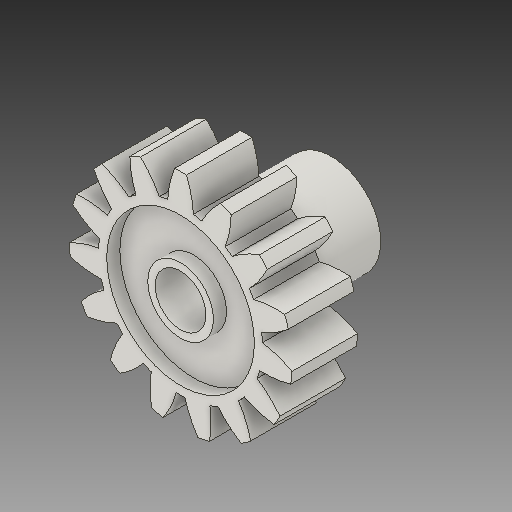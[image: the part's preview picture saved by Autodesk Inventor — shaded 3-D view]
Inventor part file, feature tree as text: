
AUTODESK INVENTOR PART (.ipt)
format: ipt  version: 2019 (Build 230136000, 136)  size: 214,016 bytes
history: imported  units: mm
features: imported_body x1
ambient origin geometry x8: Origin, YZ Plane, XZ Plane, XY Plane, X Axis, Y Axis, Z Axis, Center Point
bodies: Solide1 (imported_parasolid), Solid1 (imported_parasolid)
feature tree (1):
  imported_body  NMx_Import_Brep_tag  [imported B-rep: ~71 faces, bbox_mm=[13.581362, 13.506962, 9.2]]
